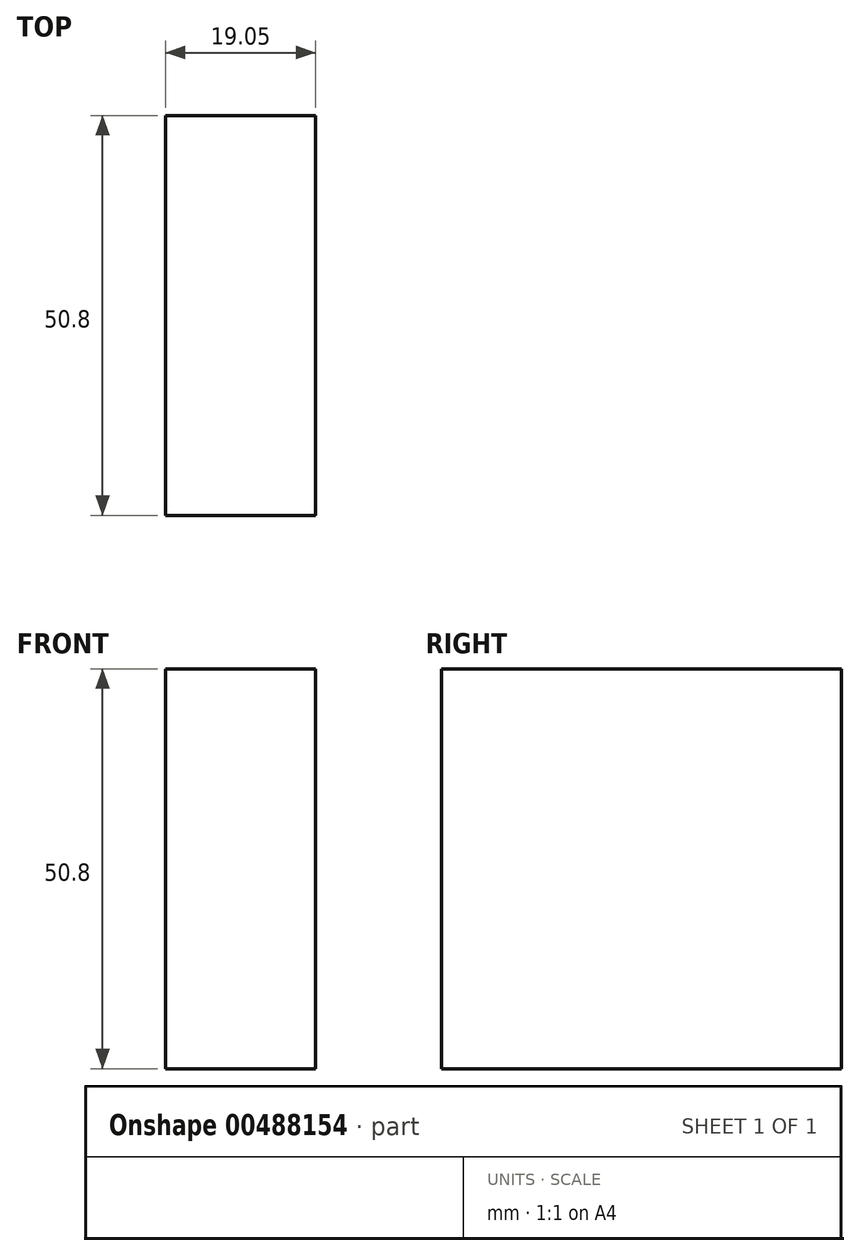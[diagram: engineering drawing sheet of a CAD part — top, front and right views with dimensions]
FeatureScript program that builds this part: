
annotation { "Feature Type Name" : "Feature", "Feature Type Description" : "" }
export const myFeature = defineFeature(function(context is Context, id is Id, definition is map)
    precondition{}
    {
        {
            var Q0;
            Q0=qCreatedBy(makeId("Front.planeOp"),FACE);
            var sketch = newSketch(context, id + "F0", { "sketchPlane" : qUnion([Q0])});
            skLineSegment(sketch, "E0", {"start": v(0, 0) * mm, "end": v(19.05, 0) * mm});
            skLineSegment(sketch, "E1", {"start": v(0, 0) * mm, "end": v(0, -50.8) * mm});
            skLineSegment(sketch, "E2", {"start": v(0, -50.8) * mm, "end": v(19.05, -50.8) * mm});
            skLineSegment(sketch, "E3", {"start": v(19.05, -50.8) * mm, "end": v(19.05, 0) * mm});
            skSolve(sketch);
        }
        {
            var Q0;
            Q0=makeQuery(id+"F0.imprint","IMPRINT",FACE,{"disambiguationData":[TD([[makeQuery(id+"F0.imprint","IMPRINT",EDGE,{"derivedFrom":sQuery(id+"F0.wireOp",EDGE,"E0")}),-1.0]])]});
            extrude(context, id + "F1", {"entities" : qUnion([Q0]), "oppositeDirection" : true, "depth" : 50.8 * mm, "offsetDistance" : 25.4 * mm});
        }
    });
